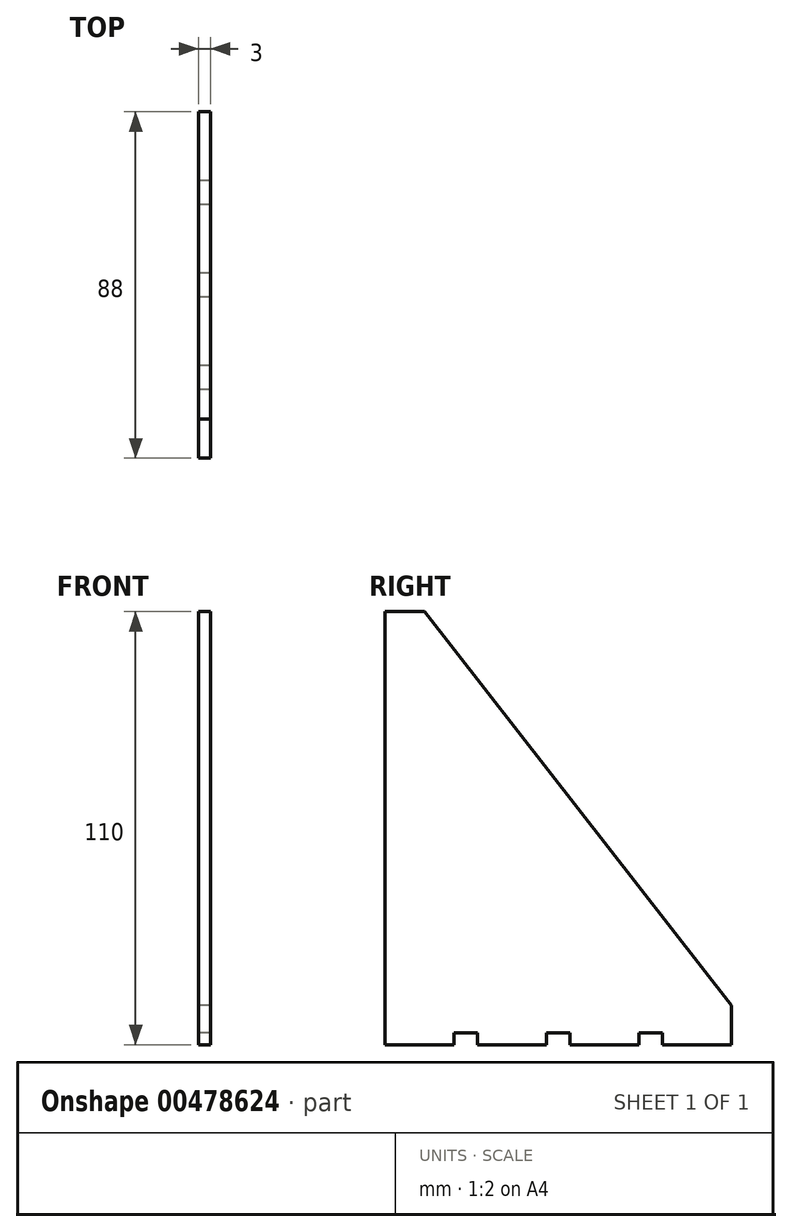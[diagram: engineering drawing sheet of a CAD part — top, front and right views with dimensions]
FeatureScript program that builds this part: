
annotation { "Feature Type Name" : "Feature", "Feature Type Description" : "" }
export const myFeature = defineFeature(function(context is Context, id is Id, definition is map)
    precondition{}
    {
        {
            var Q0;
            Q0=qCreatedBy(makeId("Right.planeOp"),FACE);
            var sketch = newSketch(context, id + "F0", { "sketchPlane" : qUnion([Q0])});
            skLineSegment(sketch, "E0", {"start": v(0, 0) * mm, "end": v(0, 110) * mm});
            skLineSegment(sketch, "E1", {"start": v(0, 0) * mm, "end": v(88, 0) * mm});
            skLineSegment(sketch, "E2", {"start": v(88, 0) * mm, "end": v(88, 10) * mm});
            skLineSegment(sketch, "E3", {"start": v(0, 110) * mm, "end": v(10, 110) * mm});
            skLineSegment(sketch, "E4", {"start": v(10, 110) * mm, "end": v(88, 10) * mm});
            skSolve(sketch);
        }
        {
            var Q0;
            Q0 = qSketchRegion(id + "F0", true);
            extrude(context, id + "F1", {"entities" : qUnion([Q0]), "depth" : 3 * mm});
        }
        {
            var Q0;
            Q0=makeQuery(id+"F1.opExtrude","CAP_FACE",FACE,{"disambiguationData":[OSD([sQuery(id+"F0.wireOp",EDGE,"E0"),sQuery(id+"F0.wireOp",EDGE,"E1"),sQuery(id+"F0.wireOp",EDGE,"E2"),sQuery(id+"F0.wireOp",EDGE,"E3"),sQuery(id+"F0.wireOp",EDGE,"E4")])],"isStart":true});
            var sketch = newSketch(context, id + "F2", { "sketchPlane" : qUnion([Q0])});
            skLineSegment(sketch, "E5", {"start": v(-44, 0) * mm, "end": v(-44, 3) * mm, "construction": true});
            skLineSegment(sketch, "E6.bottom", {"start": v(-41, 3) * mm, "end": v(-47, 3) * mm});
            skLineSegment(sketch, "E6.top", {"start": v(-41, 0) * mm, "end": v(-47, 0) * mm});
            skLineSegment(sketch, "E6.left", {"start": v(-41, 3) * mm, "end": v(-41, 0) * mm});
            skLineSegment(sketch, "E6.right", {"start": v(-47, 3) * mm, "end": v(-47, 0) * mm});
            skPoint(sketch, "E6.middle", {"position": v(-44, 1.5) * mm});
            skLineSegment(sketch, "E7", {"start": v(-41, 0) * mm, "end": v(0, 0) * mm, "construction": true});
            skLineSegment(sketch, "E8", {"start": v(0, 0) * mm, "end": v(-20.5, 0) * mm, "construction": true});
            skLineSegment(sketch, "E9", {"start": v(-20.5, 0) * mm, "end": v(-20.5, 3) * mm, "construction": true});
            skLineSegment(sketch, "E10.bottom", {"start": v(-17.5, 3) * mm, "end": v(-23.5, 3) * mm});
            skLineSegment(sketch, "E10.top", {"start": v(-17.5, 0) * mm, "end": v(-23.5, 0) * mm});
            skLineSegment(sketch, "E10.left", {"start": v(-17.5, 3) * mm, "end": v(-17.5, 0) * mm});
            skLineSegment(sketch, "E10.right", {"start": v(-23.5, 3) * mm, "end": v(-23.5, 0) * mm});
            skPoint(sketch, "E10.middle", {"position": v(-20.5, 1.5) * mm});
            skLineSegment(sketch, "E11.MirrorCS", {"start": v(-70.5, 3) * mm, "end": v(-64.5, 3) * mm});
            skLineSegment(sketch, "E12.MirrorCS", {"start": v(-64.5, 3) * mm, "end": v(-64.5, 0) * mm});
            skLineSegment(sketch, "E13.MirrorCS", {"start": v(-70.5, 3) * mm, "end": v(-70.5, 0) * mm});
            skLineSegment(sketch, "E14", {"start": v(-70.5, 0) * mm, "end": v(-64.5, 0) * mm});
            skSolve(sketch);
        }
        {
            var Q0;
            Q0 = qSketchRegion(id + "F2", true);
            extrude(context, id + "F3", {"entities" : qUnion([Q0]), "operationType" : NewBodyOperationType.REMOVE, "oppositeDirection" : true, "depth" : 25 * mm});
        }
    });
